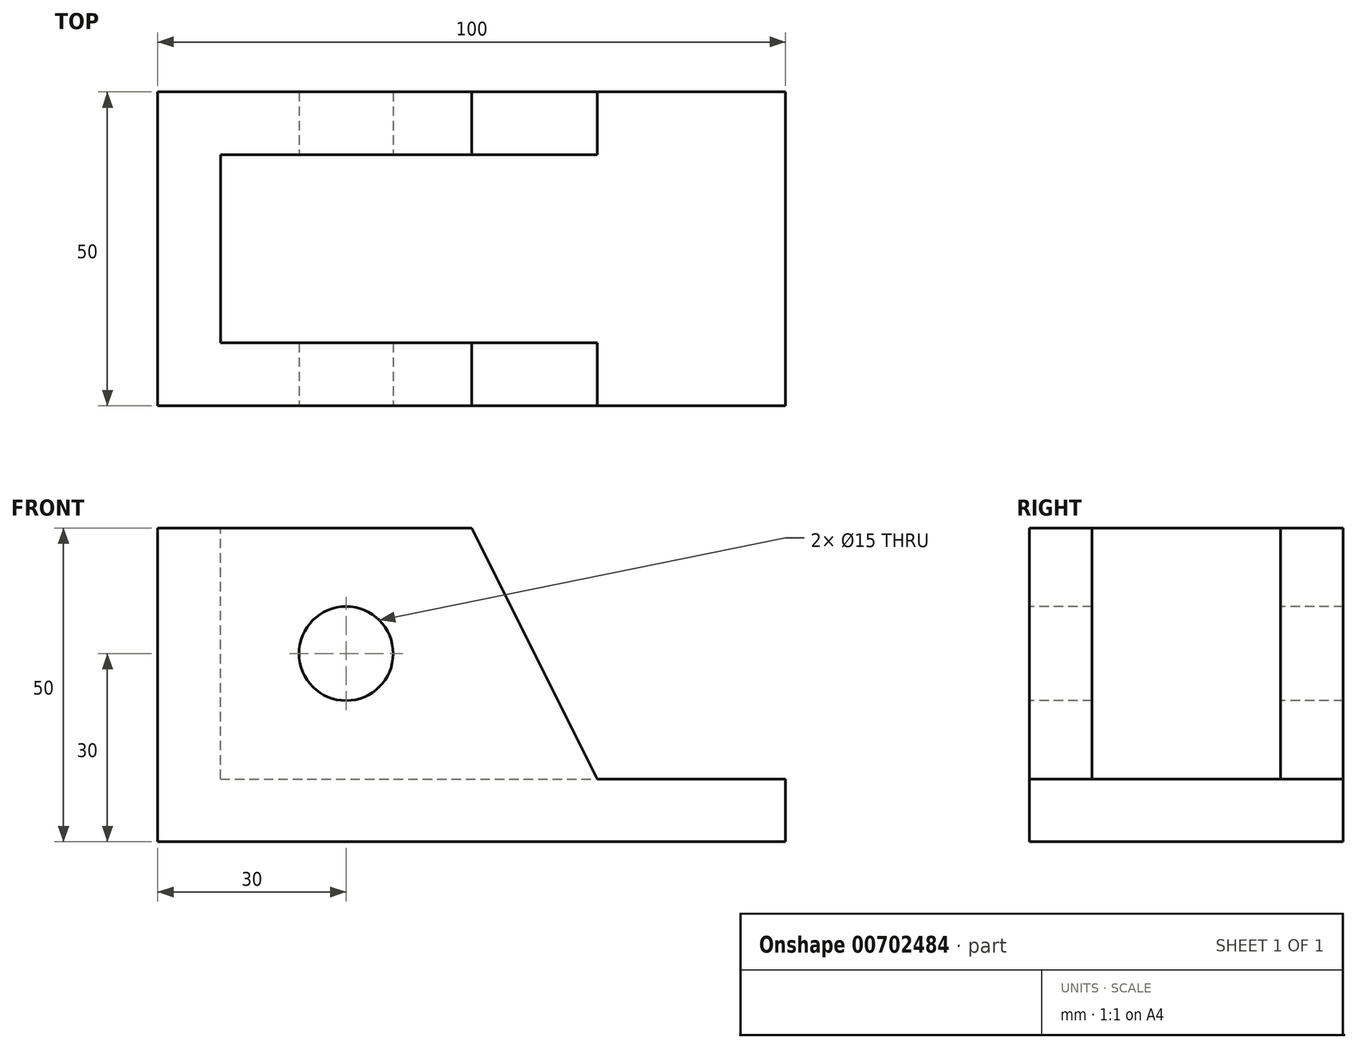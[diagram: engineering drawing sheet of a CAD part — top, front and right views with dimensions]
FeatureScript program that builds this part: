
annotation { "Feature Type Name" : "Feature", "Feature Type Description" : "" }
export const myFeature = defineFeature(function(context is Context, id is Id, definition is map)
    precondition{}
    {
        {
            var Q0;
            Q0=qCreatedBy(makeId("Front.planeOp"),FACE);
            var sketch = newSketch(context, id + "F0", { "sketchPlane" : qUnion([Q0])});
            skLineSegment(sketch, "E0.bottom", {"start": v(0, 0) * mm, "end": v(100, 0) * mm});
            skLineSegment(sketch, "E0.top", {"start": v(0, 50) * mm, "end": v(100, 50) * mm});
            skLineSegment(sketch, "E0.left", {"start": v(0, 0) * mm, "end": v(0, 50) * mm});
            skLineSegment(sketch, "E0.right", {"start": v(100, 0) * mm, "end": v(100, 50) * mm});
            skSolve(sketch);
        }
        {
            var Q0;
            Q0=makeQuery(id+"F0.imprint","IMPRINT",FACE,{"disambiguationData":[TD([[makeQuery(id+"F0.imprint","IMPRINT",EDGE,{"derivedFrom":sQuery(id+"F0.wireOp",EDGE,"E0.bottom")}),1.0]])]});
            extrude(context, id + "F1", {"entities" : qUnion([Q0]), "oppositeDirection" : true, "depth" : 50 * mm, "offsetDistance" : 25 * mm});
        }
        {
            var Q0;
            Q0=makeQuery(id+"F1.opExtrude","SWEPT_FACE",FACE,{"disambiguationData":[OSD([sQuery(id+"F0.wireOp",EDGE,"E0.top")])]});
            var sketch = newSketch(context, id + "F2", { "sketchPlane" : qUnion([Q0])});
            skLineSegment(sketch, "E1", {"start": v(0, 25) * mm, "end": v(171.1, 25) * mm, "construction": true});
            skLineSegment(sketch, "E2.bottom", {"start": v(10, 10) * mm, "end": v(100, 10) * mm});
            skLineSegment(sketch, "E2.top", {"start": v(10, 40) * mm, "end": v(100, 40) * mm});
            skLineSegment(sketch, "E2.left", {"start": v(10, 10) * mm, "end": v(10, 40) * mm});
            skLineSegment(sketch, "E2.right", {"start": v(100, 10) * mm, "end": v(100, 40) * mm});
            skSolve(sketch);
        }
        {
            var Q0;
            Q0=makeQuery(id+"F2.imprint","IMPRINT",FACE,{"disambiguationData":[TD([[makeQuery(id+"F2.imprint","IMPRINT",EDGE,{"derivedFrom":sQuery(id+"F2.wireOp",EDGE,"E2.bottom")}),1.0]])]});
            extrude(context, id + "F3", {"entities" : qUnion([Q0]), "operationType" : NewBodyOperationType.REMOVE, "oppositeDirection" : true, "depth" : 40 * mm, "offsetDistance" : 25 * mm});
        }
        {
            var Q0;
            Q0=makeQuery(id+"F1.opExtrude","CAP_FACE",FACE,{"disambiguationData":[OSD([sQuery(id+"F0.wireOp",EDGE,"E0.bottom"),sQuery(id+"F0.wireOp",EDGE,"E0.top"),sQuery(id+"F0.wireOp",EDGE,"E0.left"),sQuery(id+"F0.wireOp",EDGE,"E0.right")])],"isStart":true});
            var sketch = newSketch(context, id + "F4", { "sketchPlane" : qUnion([Q0])});
            skLineSegment(sketch, "E3", {"start": v(0, 30) * mm, "end": v(132.56, 30) * mm, "construction": true});
            skLineSegment(sketch, "E4", {"start": v(30, 0) * mm, "end": v(30, 74) * mm, "construction": true});
            skCircle(sketch, "E5", {"center": v(30, 30) * mm, "radius": 7.5 * mm});
            skSolve(sketch);
        }
        {
            var Q0;
            Q0=makeQuery(id+"F4.imprint","IMPRINT",FACE,{"disambiguationData":[TD([[makeQuery(id+"F4.imprint","IMPRINT",EDGE,{"derivedFrom":sQuery(id+"F4.wireOp",EDGE,"E5")}),1.0]])]});
            extrude(context, id + "F5", {"entities" : qUnion([Q0]), "operationType" : NewBodyOperationType.REMOVE, "endBound" : BoundingType.THROUGH_ALL, "oppositeDirection" : true, "depth" : 25 * mm, "offsetDistance" : 25 * mm});
        }
        {
            var Q0;
            Q0=makeQuery(id+"F1.opExtrude","CAP_FACE",FACE,{"disambiguationData":[OSD([sQuery(id+"F0.wireOp",EDGE,"E0.bottom"),sQuery(id+"F0.wireOp",EDGE,"E0.top"),sQuery(id+"F0.wireOp",EDGE,"E0.left"),sQuery(id+"F0.wireOp",EDGE,"E0.right")])],"isStart":true});
            var sketch = newSketch(context, id + "F6", { "sketchPlane" : qUnion([Q0])});
            skLineSegment(sketch, "E6", {"start": v(50, 50) * mm, "end": v(100, 50) * mm});
            skLineSegment(sketch, "E7", {"start": v(100, 50) * mm, "end": v(100, 10) * mm});
            skLineSegment(sketch, "E8", {"start": v(100, 10) * mm, "end": v(70, 10) * mm});
            skLineSegment(sketch, "E9", {"start": v(70, 10) * mm, "end": v(50, 50) * mm});
            skSolve(sketch);
        }
        {
            var Q0;
            Q0=makeQuery(id+"F6.imprint","IMPRINT",FACE,{"disambiguationData":[TD([[makeQuery(id+"F6.imprint","IMPRINT",EDGE,{"derivedFrom":sQuery(id+"F6.wireOp",EDGE,"E6")}),-1.0]])]});
            extrude(context, id + "F7", {"entities" : qUnion([Q0]), "operationType" : NewBodyOperationType.REMOVE, "endBound" : BoundingType.THROUGH_ALL, "oppositeDirection" : true, "depth" : 25 * mm, "offsetDistance" : 25 * mm});
        }
    });
